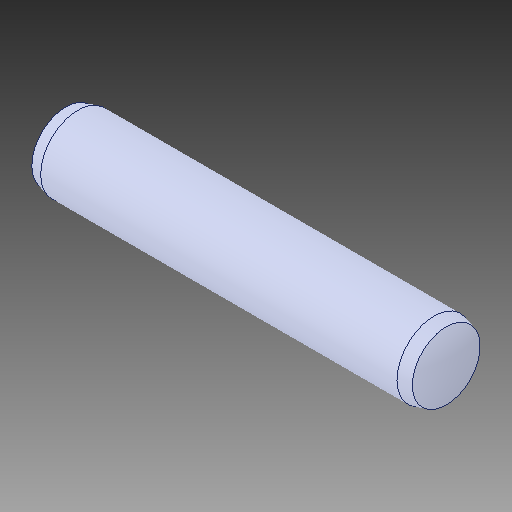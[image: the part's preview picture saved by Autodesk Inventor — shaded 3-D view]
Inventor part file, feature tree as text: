
AUTODESK INVENTOR PART (.ipt)
format: ipt  version: 2019 (Build 230136000, 136)  size: 96,256 bytes
history: native  units: in
note: dims shown in document units (in); Inventor stores cm internally (conversion verified against a paired STEP export)
features: mirror x1
ambient origin geometry x8: Origin, YZ Plane, XZ Plane, XY Plane, X Axis, Y Axis, Z Axis, Center Point
bodies: Solid1 (feature_tree)
feature tree (1):
  mirror  "Mirror1"
